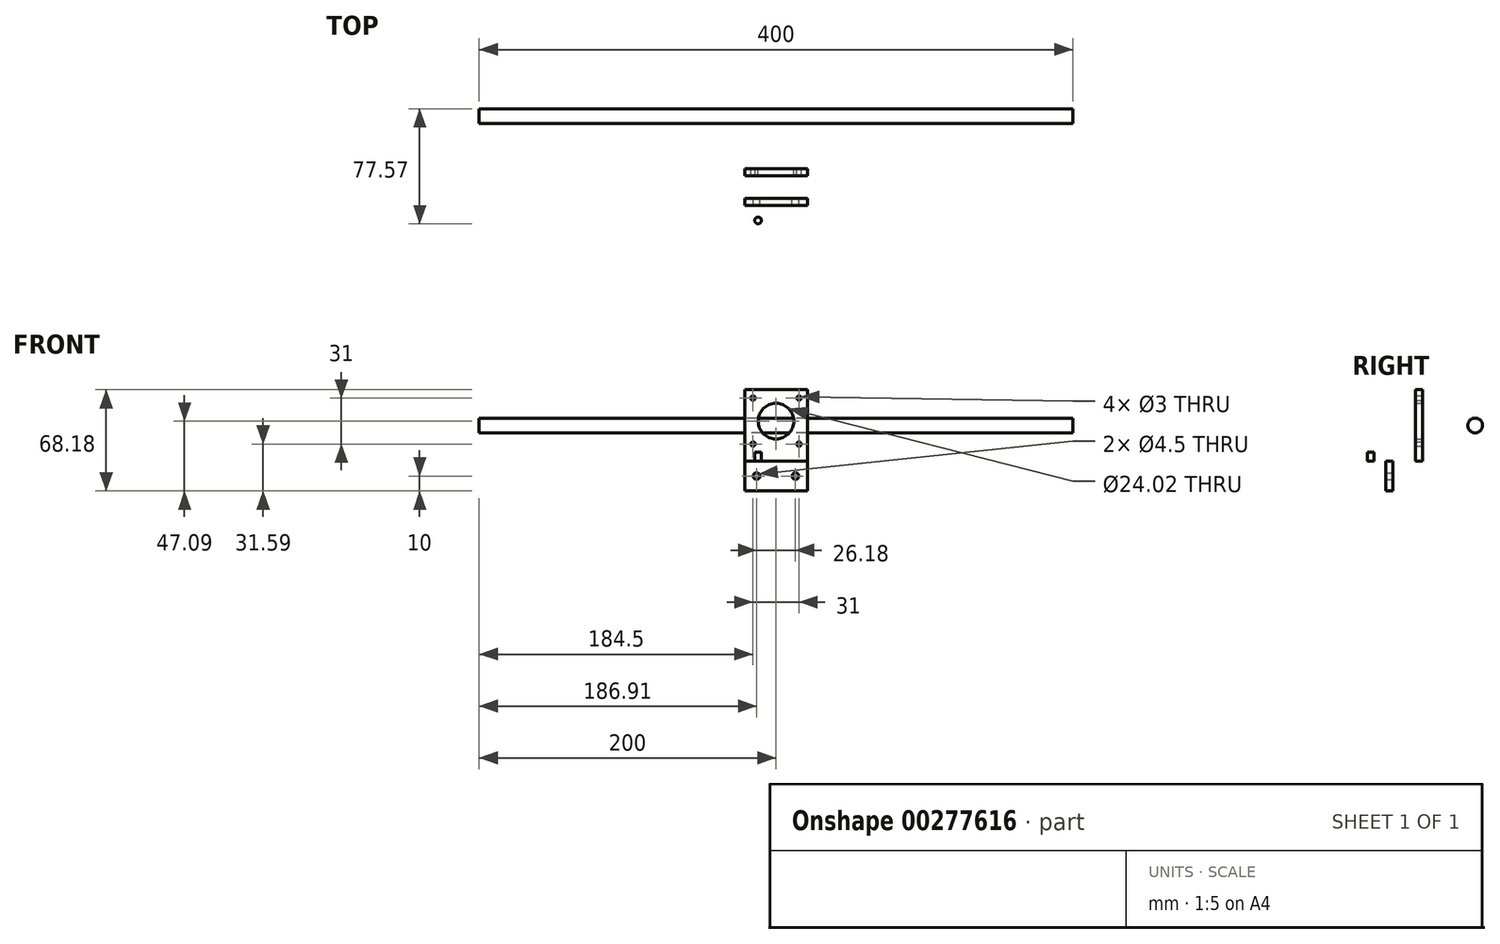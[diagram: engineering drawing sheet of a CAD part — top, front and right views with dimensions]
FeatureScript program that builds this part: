
annotation { "Feature Type Name" : "Feature", "Feature Type Description" : "" }
export const myFeature = defineFeature(function(context is Context, id is Id, definition is map)
    precondition{}
    {
        {
            var Q0;
            Q0=qCreatedBy(makeId("Front.planeOp"),FACE);
            var sketch = newSketch(context, id + "F0", { "sketchPlane" : qUnion([Q0])});
            skLineSegment(sketch, "E0.bottom", {"start": v(21.1, -24.09) * mm, "end": v(-21.09, -24.1) * mm});
            skLineSegment(sketch, "E0.top", {"start": v(21.09, 24.1) * mm, "end": v(-21.1, 24.09) * mm});
            skLineSegment(sketch, "E0.left", {"start": v(21.1, -24.09) * mm, "end": v(21.09, 24.1) * mm});
            skLineSegment(sketch, "E0.right", {"start": v(-21.09, -24.1) * mm, "end": v(-21.1, 24.09) * mm});
            skPoint(sketch, "E0.middle", {"position": v(0, 0) * mm});
            skLineSegment(sketch, "E1.top", {"start": v(21.1, -18.09) * mm, "end": v(-21.09, -18.1) * mm});
            skLineSegment(sketch, "E1.left", {"start": v(21.09, 24.1) * mm, "end": v(21.1, -18.09) * mm});
            skLineSegment(sketch, "E1.right", {"start": v(-21.1, 24.09) * mm, "end": v(-21.09, -18.1) * mm});
            skLineSegment(sketch, "E2", {"start": v(0, 33.2) * mm, "end": v(0, -36.54) * mm, "construction": true});
            skLineSegment(sketch, "E3", {"start": v(-39.86, 3) * mm, "end": v(39.2, 3) * mm, "construction": true});
            skLineSegment(sketch, "E4", {"start": v(-21.1, 24.09) * mm, "end": v(21.1, -18.09) * mm, "construction": true});
            skLineSegment(sketch, "E5", {"start": v(21.09, 24.1) * mm, "end": v(-21.09, -18.1) * mm, "construction": true});
            skCircle(sketch, "E6", {"center": v(-15.5, 18.5) * mm, "radius": 1.5 * mm});
            skCircle(sketch, "E7", {"center": v(15.5, 18.5) * mm, "radius": 1.5 * mm});
            skCircle(sketch, "E8", {"center": v(15.5, -12.5) * mm, "radius": 1.5 * mm});
            skCircle(sketch, "E9", {"center": v(-15.5, -12.5) * mm, "radius": 1.5 * mm});
            skCircle(sketch, "E10", {"center": v(0, 3) * mm, "radius": 12 * mm});
            skSolve(sketch);
        }
        {
            var Q0;
            Q0 = qSketchRegion(id + "F0", true);
            extrude(context, id + "F1", {"entities" : qUnion([Q0]), "depth" : 5 * mm});
        }
        {
            var Q0;
            Q0=makeQuery(id+"F1.opExtrude","CAP_FACE",FACE,{"disambiguationData":[OSD([sQuery(id+"F0.wireOp",EDGE,"E0.bottom"),sQuery(id+"F0.wireOp",EDGE,"E0.left"),sQuery(id+"F0.wireOp",EDGE,"E0.right"),sQuery(id+"F0.wireOp",EDGE,"E0.top"),sQuery(id+"F0.wireOp",EDGE,"E1.left"),sQuery(id+"F0.wireOp",EDGE,"E1.right"),sQuery(id+"F0.wireOp",EDGE,"E6"),sQuery(id+"F0.wireOp",EDGE,"E7"),sQuery(id+"F0.wireOp",EDGE,"E8"),sQuery(id+"F0.wireOp",EDGE,"E9")])],"isStart":false});
            var sketch = newSketch(context, id + "F2", { "sketchPlane" : qUnion([Q0])});
            skLineSegment(sketch, "E11.bottom", {"start": v(-21.09, -24.09) * mm, "end": v(21.1, -24.09) * mm});
            skLineSegment(sketch, "E11.top", {"start": v(-21.09, -18.1) * mm, "end": v(21.1, -18.1) * mm});
            skLineSegment(sketch, "E11.left", {"start": v(-21.09, -24.09) * mm, "end": v(-21.09, -18.1) * mm});
            skLineSegment(sketch, "E11.right", {"start": v(21.1, -24.09) * mm, "end": v(21.1, -18.1) * mm});
            skSolve(sketch);
        }
        {
            var Q0;
            Q0=makeQuery(id+"F2.imprint","IMPRINT",FACE,{"disambiguationData":[TD([[makeQuery(id+"F2.imprint","IMPRINT",EDGE,{"derivedFrom":sQuery(id+"F2.wireOp",EDGE,"E11.bottom")}),-1.0]])]});
            extrude(context, id + "F3", {"entities" : qUnion([Q0]), "operationType" : NewBodyOperationType.ADD, "depth" : 40 * mm});
        }
        {
            var Q0;
            Q0=makeQuery(id+"F3.opExtrude","SWEPT_FACE",FACE,{"disambiguationData":[OSD([sQuery(id+"F2.wireOp",EDGE,"E11.top")])]});
            var sketch = newSketch(context, id + "F4", { "sketchPlane" : qUnion([Q0])});
            skCircle(sketch, "E12", {"center": v(12.12, -35) * mm, "radius": 2.25 * mm});
            skCircle(sketch, "E13.MirrorC", {"center": v(-12.12, -35) * mm, "radius": 2.25 * mm});
            skSolve(sketch);
        }
        {
            var Q0;
            Q0=makeQuery(id+"F4.imprint","IMPRINT",FACE,{"disambiguationData":[TD([[makeQuery(id+"F4.imprint","IMPRINT",EDGE,{"derivedFrom":sQuery(id+"F4.wireOp",EDGE,"E13.MirrorC")}),-1.0]])]});
            var Q1;
            Q1=makeQuery(id+"F4.imprint","IMPRINT",FACE,{"disambiguationData":[TD([[makeQuery(id+"F4.imprint","IMPRINT",EDGE,{"derivedFrom":sQuery(id+"F4.wireOp",EDGE,"E12")}),1.0]])]});
            extrude(context, id + "F5", {"entities" : qUnion([Q0, Q1]), "operationType" : NewBodyOperationType.REMOVE, "endBound" : BoundingType.UP_TO_NEXT, "oppositeDirection" : true, "depth" : 25 * mm});
        }
        {
            var Q0;
            Q0=makeQuery(id+"F3.opExtrude","SWEPT_FACE",FACE,{"disambiguationData":[OSD([sQuery(id+"F2.wireOp",EDGE,"E11.top")])]});
            var sketch = newSketch(context, id + "F6", { "sketchPlane" : qUnion([Q0])});
            skCircle(sketch, "E14", {"center": v(-12.12, -35) * mm, "radius": 4 * mm});
            skCircle(sketch, "E15.MirrorC", {"center": v(12.12, -35) * mm, "radius": 4 * mm});
            skSolve(sketch);
        }
        {
            var Q0;
            Q0=makeQuery(id+"F6.imprint","IMPRINT",FACE,{"disambiguationData":[TD([[makeQuery(id+"F6.imprint","IMPRINT",EDGE,{"derivedFrom":sQuery(id+"F6.wireOp",EDGE,"E14")}),1.0]])]});
            var Q1;
            Q1=makeQuery(id+"F6.imprint","IMPRINT",FACE,{"disambiguationData":[TD([[makeQuery(id+"F6.imprint","IMPRINT",EDGE,{"derivedFrom":sQuery(id+"F6.wireOp",EDGE,"E15.MirrorC")}),-1.0]])]});
            extrude(context, id + "F7", {"entities" : qUnion([Q0, Q1]), "operationType" : NewBodyOperationType.REMOVE, "oppositeDirection" : true, "depth" : 5 * mm});
        }
        {
            var Q0;
            Q0=makeQuery(id+"F3.boolean.opBoolean","MERGE",FACE,{"derivedFrom":[makeQuery(id+"F1.opExtrude","SWEPT_FACE",FACE,{"disambiguationData":[OSD([sQuery(id+"F0.wireOp",EDGE,"E0.bottom")])]}),makeQuery(id+"F3.opExtrude","SWEPT_FACE",FACE,{"disambiguationData":[OSD([sQuery(id+"F2.wireOp",EDGE,"E11.bottom")])]})]});
            var sketch = newSketch(context, id + "F8", { "sketchPlane" : qUnion([Q0])});
            skLineSegment(sketch, "E16.bottom", {"start": v(-21.1, 25) * mm, "end": v(21.09, 25) * mm});
            skLineSegment(sketch, "E16.top", {"start": v(-21.1, 20) * mm, "end": v(21.09, 20) * mm});
            skLineSegment(sketch, "E16.left", {"start": v(-21.1, 25) * mm, "end": v(-21.1, 20) * mm});
            skLineSegment(sketch, "E16.right", {"start": v(21.09, 25) * mm, "end": v(21.09, 20) * mm});
            skSolve(sketch);
        }
        {
            var Q0;
            Q0=makeQuery(id+"F8.imprint","IMPRINT",FACE,{"disambiguationData":[TD([[makeQuery(id+"F8.imprint","IMPRINT",EDGE,{"derivedFrom":sQuery(id+"F8.wireOp",EDGE,"E16.bottom")}),-1.0]])]});
            extrude(context, id + "F9", {"entities" : qUnion([Q0]), "operationType" : NewBodyOperationType.ADD, "depth" : 20 * mm});
        }
        {
            var Q0;
            Q0=makeQuery(id+"F9.opExtrude","SWEPT_FACE",FACE,{"disambiguationData":[OSD([sQuery(id+"F8.wireOp",EDGE,"E16.top")])]});
            var sketch = newSketch(context, id + "F10", { "sketchPlane" : qUnion([Q0])});
            skCircle(sketch, "E17", {"center": v(13.09, -34.1) * mm, "radius": 2.25 * mm});
            skCircle(sketch, "E18.MirrorC", {"center": v(-13.09, -34.1) * mm, "radius": 2.25 * mm});
            skSolve(sketch);
        }
        {
            var Q0;
            Q0 = qSketchRegion(id + "F12", true);
            var Q1;
            Q1 = qSketchRegion(id + "F10", true);
            extrude(context, id + "F11", {"entities" : qUnion([Q0, Q1]), "operationType" : NewBodyOperationType.REMOVE, "endBound" : BoundingType.UP_TO_NEXT, "oppositeDirection" : true, "depth" : 25 * mm});
        }
        {
            var Q0;
            Q0=qCreatedBy(makeId("Right.planeOp"),FACE);
            var sketch = newSketch(context, id + "F12", { "sketchPlane" : qUnion([Q0])});
            skCircle(sketch, "E19", {"center": v(35.32, 0) * mm, "radius": 5 * mm});
            skSolve(sketch);
        }
        {
            var Q0;
            Q0=makeQuery(id+"F12.imprint","IMPRINT",FACE,{"disambiguationData":[TD([[makeQuery(id+"F12.imprint","IMPRINT",EDGE,{"derivedFrom":sQuery(id+"F12.wireOp",EDGE,"E19")}),1.0]])]});
            extrude(context, id + "F13", {"entities" : qUnion([Q0]), "endBound" : BoundingType.SYMMETRIC, "depth" : 400 * mm});
        }
    });
